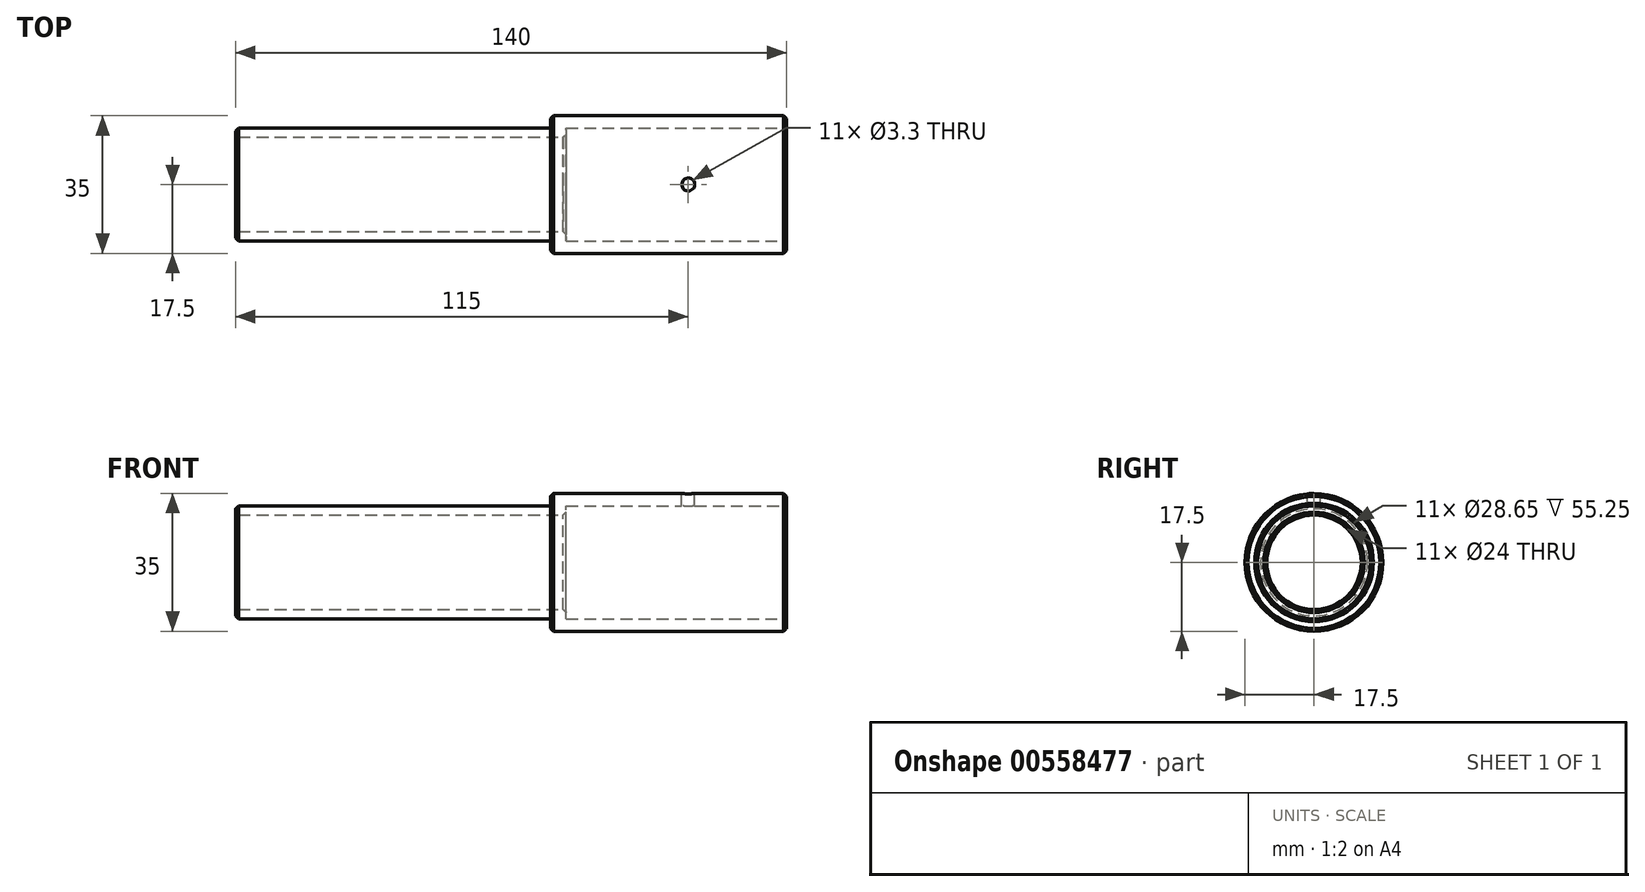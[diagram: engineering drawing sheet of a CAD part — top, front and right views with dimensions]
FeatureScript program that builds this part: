
annotation { "Feature Type Name" : "Feature", "Feature Type Description" : "" }
export const myFeature = defineFeature(function(context is Context, id is Id, definition is map)
    precondition{}
    {
        {
            var Q0;
            Q0=qCreatedBy(makeId("Front.planeOp"),FACE);
            var sketch = newSketch(context, id + "F0", { "sketchPlane" : qUnion([Q0])});
            skLineSegment(sketch, "E0", {"start": v(0, 17.5) * mm, "end": v(-60, 17.5) * mm});
            skLineSegment(sketch, "E1", {"start": v(-60, 17.5) * mm, "end": v(-60, 14.32) * mm});
            skLineSegment(sketch, "E2", {"start": v(-60, 14.32) * mm, "end": v(-140, 14.32) * mm});
            skLineSegment(sketch, "E3", {"start": v(-140, 14.32) * mm, "end": v(-140, 12) * mm});
            skLineSegment(sketch, "E4", {"start": v(-140, 12) * mm, "end": v(-56, 12) * mm});
            skLineSegment(sketch, "E5", {"start": v(-56, 12) * mm, "end": v(-56, 14.32) * mm});
            skLineSegment(sketch, "E6", {"start": v(-56, 14.32) * mm, "end": v(0, 14.33) * mm});
            skLineSegment(sketch, "E7", {"start": v(0, 14.33) * mm, "end": v(0, 17.5) * mm});
            skLineSegment(sketch, "E8", {"start": v(19.52, 0) * mm, "end": v(-166.53, 0) * mm, "construction": true});
            skSolve(sketch);
        }
        {
            var Q0;
            Q0 = qSketchRegion(id + "F0", true);
            var Q1;
            Q1=sQuery(id+"F0.wireOp",EDGE,"E8");
            revolve(context, id + "F1", {"entities" : qUnion([Q0]), "axis" : qUnion([Q1]), "revolveType" : RevolveType.FULL});
        }
        {
            var Q0;
            Q0=qCreatedBy(makeId("Top.planeOp"),FACE);
            cPlane(context, id + "F2", {"entities" : qUnion([Q0]), "cplaneType" : CPlaneType.OFFSET, "offset" : (35 / 2) * mm, "width" : 150 * mm, "height" : 150 * mm});
        }
        {
            var Q0;
            Q0=qCreatedBy(id+"F2.planeOp",FACE);
            var sketch = newSketch(context, id + "F3", { "sketchPlane" : qUnion([Q0])});
            skPoint(sketch, "E9", {"position": v(-25, 0) * mm});
            skSolve(sketch);
        }
        {
            var Q0;
            Q0=sQuery(id+"F3.wireOp",VERTEX,"E9");
            var Q1;
            Q1=makeQuery(id+"F1.opRevolve","SWEPT_BODY",BODY,{"disambiguationData":[OSD([sQuery(id+"F0.wireOp",EDGE,"E0"),sQuery(id+"F0.wireOp",EDGE,"E1"),sQuery(id+"F0.wireOp",EDGE,"E2"),sQuery(id+"F0.wireOp",EDGE,"E3"),sQuery(id+"F0.wireOp",EDGE,"E4"),sQuery(id+"F0.wireOp",EDGE,"E5"),sQuery(id+"F0.wireOp",EDGE,"E6"),sQuery(id+"F0.wireOp",EDGE,"E7")])]});
            hole(context, id + "F4", {"style" : HoleStyle.SIMPLE, "endStyle" : HoleEndStyle.BLIND, "standardTappedOrClearance" : lookupTablePath({ "standard" : "ISO", "engagement" : "75%", "pitch" : "0.7 mm", "size" : "M4", "type" : "Tapped" }), "standardBlindInLast" : lookupTablePath({ "standard" : "ISO", "engagement" : "75%", "pitch" : "0.7 mm", "size" : "M4", "type" : "Tapped" }), "holeDiameter" : 3.3 * mm, "showTappedDepth" : true, "holeDepth" : 8.1 * mm, "tappedDepth" : 6 * mm, "tapClearance" : 3, "locations" : qUnion([Q0]), "scope" : qUnion([Q1]), "majorDiameter" : 4 * mm});
        }
        {
            var Q0;
            Q0=makeQuery(id+"F1.opRevolve","SWEPT_EDGE",EDGE,{"disambiguationData":[OSD([sQuery(id+"F0.wireOp",EDGE,"E2"),sQuery(id+"F0.wireOp",EDGE,"E3")])]});
            var Q1;
            Q1=makeQuery(id+"F1.opRevolve","SWEPT_EDGE",EDGE,{"disambiguationData":[OSD([sQuery(id+"F0.wireOp",EDGE,"E3"),sQuery(id+"F0.wireOp",EDGE,"E4")])]});
            var Q2;
            Q2=makeQuery(id+"F1.opRevolve","SWEPT_EDGE",EDGE,{"disambiguationData":[OSD([sQuery(id+"F0.wireOp",EDGE,"E0"),sQuery(id+"F0.wireOp",EDGE,"E1")])]});
            var Q3;
            Q3=makeQuery(id+"F1.opRevolve","SWEPT_EDGE",EDGE,{"disambiguationData":[OSD([sQuery(id+"F0.wireOp",EDGE,"E0"),sQuery(id+"F0.wireOp",EDGE,"E7")])]});
            var Q4;
            Q4=makeQuery(id+"F1.opRevolve","SWEPT_EDGE",EDGE,{"disambiguationData":[OSD([sQuery(id+"F0.wireOp",EDGE,"E6"),sQuery(id+"F0.wireOp",EDGE,"E7")])]});
            var Q5;
            Q5=makeQuery(id+"F1.opRevolve","SWEPT_EDGE",EDGE,{"disambiguationData":[OSD([sQuery(id+"F0.wireOp",EDGE,"E4"),sQuery(id+"F0.wireOp",EDGE,"E5")])]});
            chamfer(context, id + "F5", {"entities" : qUnion([Q0, Q1, Q2, Q3, Q4, Q5]), "width" : 0.75 * mm, "tangentPropagation" : true});
        }
    });
